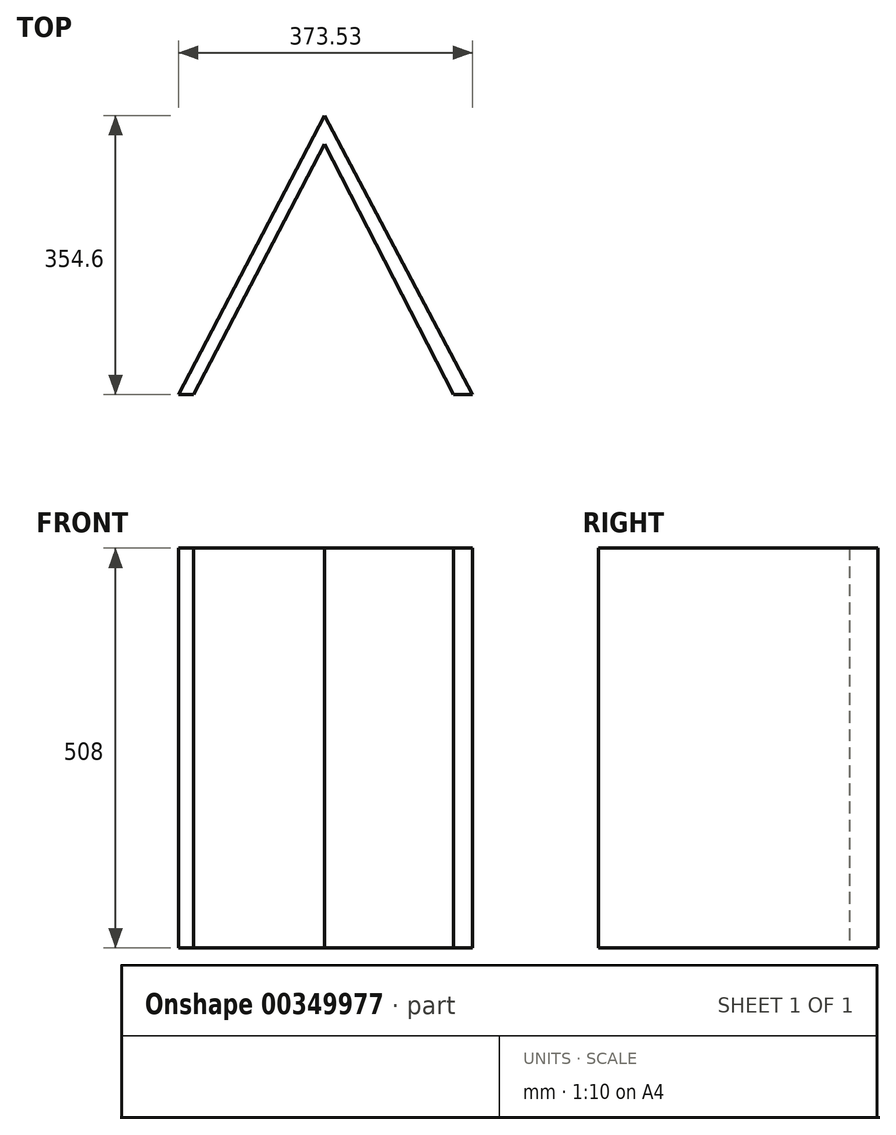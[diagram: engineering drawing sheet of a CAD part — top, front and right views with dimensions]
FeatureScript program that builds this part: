
annotation { "Feature Type Name" : "Feature", "Feature Type Description" : "" }
export const myFeature = defineFeature(function(context is Context, id is Id, definition is map)
    precondition{}
    {
        {
            var Q0;
            Q0=qCreatedBy(makeId("Top.planeOp"),FACE);
            var sketch = newSketch(context, id + "F0", { "sketchPlane" : qUnion([Q0])});
            skLineSegment(sketch, "E0", {"start": v(0, 175.4) * mm, "end": v(-185.5, -179.2) * mm});
            skLineSegment(sketch, "E1", {"start": v(-185.5, -179.2) * mm, "end": v(-166.57, -179.2) * mm});
            skLineSegment(sketch, "E2", {"start": v(-166.57, -179.2) * mm, "end": v(0, 139.22) * mm});
            skLineSegment(sketch, "E3", {"start": v(0, 139.22) * mm, "end": v(0, 175.4) * mm});
            skLineSegment(sketch, "E4", {"start": v(0, 175.4) * mm, "end": v(188.03, -179.2) * mm});
            skLineSegment(sketch, "E5", {"start": v(188.03, -179.2) * mm, "end": v(164.05, -179.2) * mm});
            skLineSegment(sketch, "E6", {"start": v(164.05, -179.2) * mm, "end": v(0, 139.22) * mm});
            skSolve(sketch);
        }
        {
            var Q0;
            Q0 = qSketchRegion(id + "F0", true);
            extrude(context, id + "F1", {"entities" : qUnion([Q0]), "depth" : 508 * mm});
        }
    });
